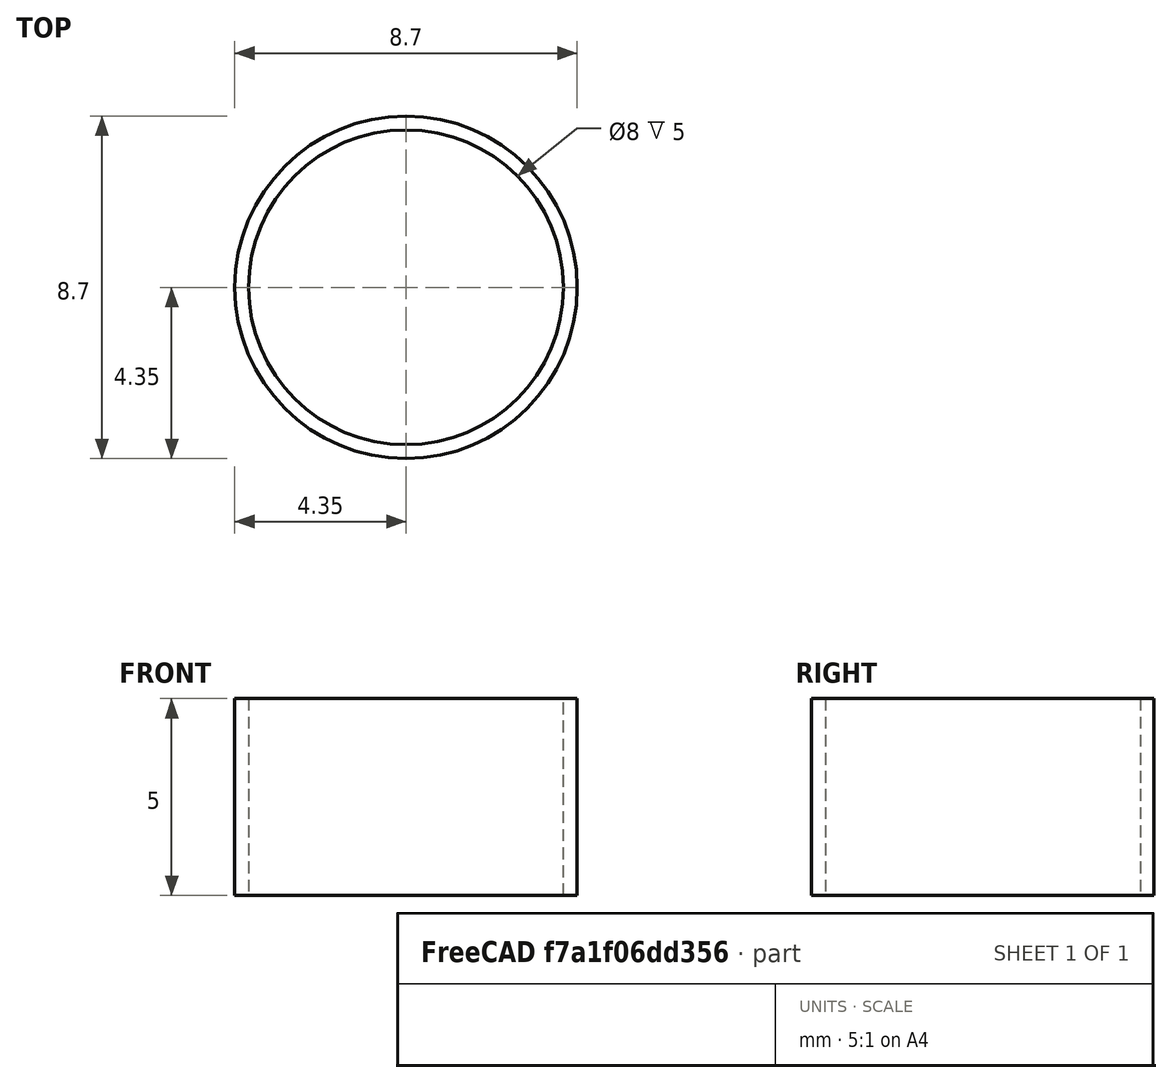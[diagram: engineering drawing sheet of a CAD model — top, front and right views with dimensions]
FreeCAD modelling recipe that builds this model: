
FCSTD DOCUMENT  (FreeCAD 0.21R33668 +26 (Git))
Label: Base_AGV
License: All rights reserved
LicenseURL: https://en.wikipedia.org/wiki/All_rights_reserved
objects: Sketcher::SketchObject×1, PartDesign::Pad×1, PartDesign::Body×1
note: 4 computed .brp shape members not serialized (recipe doc carries the construction recipe); baked Part::Feature solids carry a one-line shape summary decoded from their .brp

FEATURE [Sketcher::SketchObject] Sketch
  FullyConstrained = true
  MapMode = 5
  Support = -> [XY_Plane]
  sketch-geometry (2):
    g0: Circle CenterX=0 CenterY=0 CenterZ=0 NormalX=0 NormalY=0 NormalZ=1 AngleXU=0 Radius=4
    g1: Circle CenterX=0 CenterY=0 CenterZ=0 NormalX=0 NormalY=0 NormalZ=1 AngleXU=0 Radius=4.35
  constraints (4):
    c: Coincident(g0,g-1)
    c: Diameter(g0) = 8
    c: Coincident(g1,g0)
    c: Diameter(g1) = 8.7
FEATURE [PartDesign::Pad] Pad
  Direction = (0,0,1)
  Length = 5
  Length2 = 10
  Profile = -> Sketch
  ReferenceAxis = -> Sketch [N_Axis]
  Type = 0
FEATURE [PartDesign::Body] Body
  Group = -> [Sketch,Pad]
  Origin = -> Origin
  Tip = -> Pad
